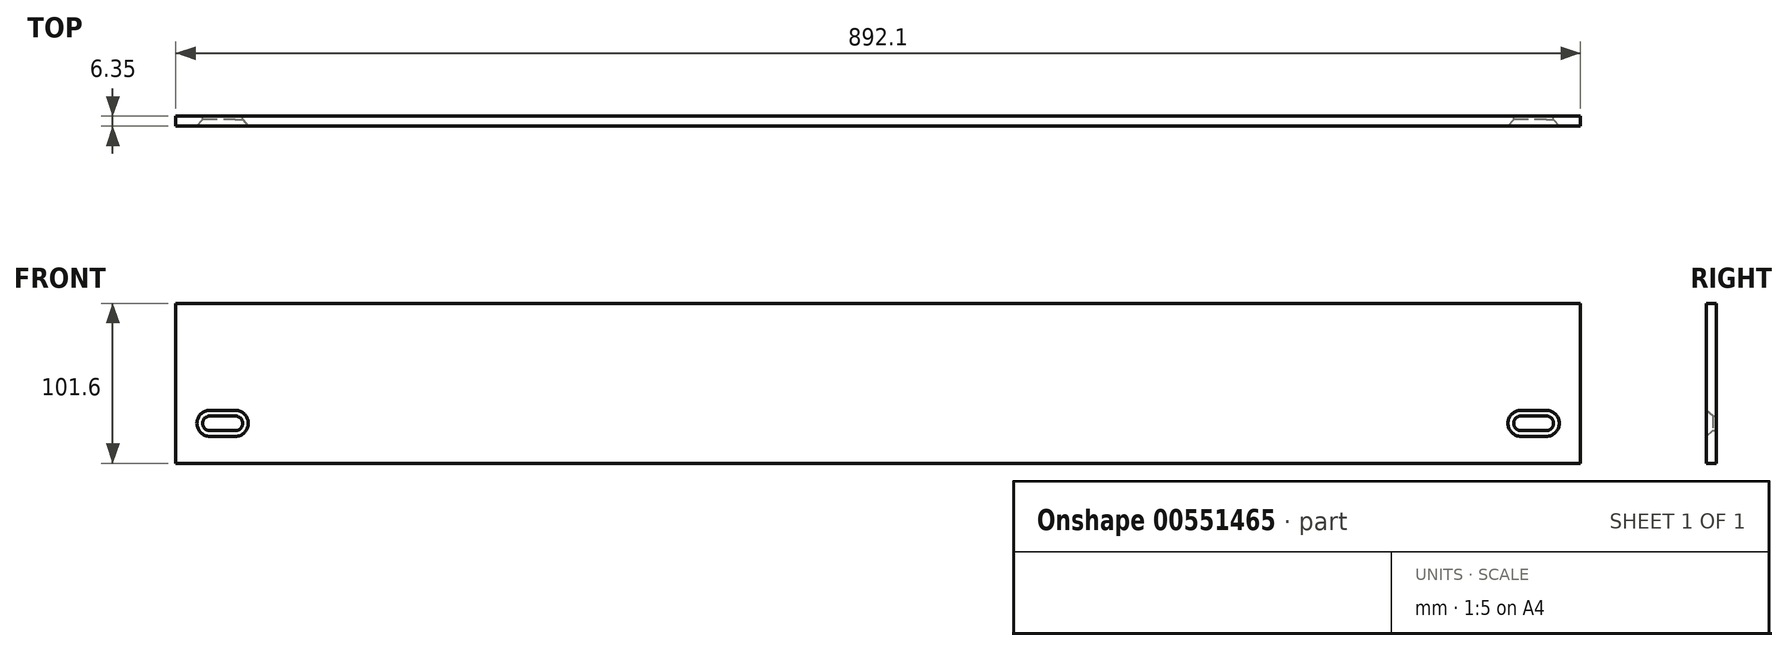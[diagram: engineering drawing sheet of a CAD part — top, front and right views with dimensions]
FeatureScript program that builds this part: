
annotation { "Feature Type Name" : "Feature", "Feature Type Description" : "" }
export const myFeature = defineFeature(function(context is Context, id is Id, definition is map)
    precondition{}
    {
        {
            var Q0;
            Q0=qCreatedBy(makeId("Front.planeOp"),FACE);
            var sketch = newSketch(context, id + "F0", { "sketchPlane" : qUnion([Q0])});
            skLineSegment(sketch, "E0", {"start": v(-446.05, -50.8) * mm, "end": v(-446.05, 50.8) * mm});
            skLineSegment(sketch, "E1", {"start": v(446.05, -50.8) * mm, "end": v(-446.05, -50.8) * mm});
            skLineSegment(sketch, "E2", {"start": v(446.05, 50.8) * mm, "end": v(-446.05, 50.8) * mm});
            skLineSegment(sketch, "E3", {"start": v(446.05, -50.8) * mm, "end": v(446.05, 50.8) * mm});
            skArc(sketch, "E4", {"start": v(-424.41, -20.76) * mm, "mid": v(-429.05, -25.4) * mm, "end": v(-424.41, -30.04) * mm});
            skArc(sketch, "E5", {"start": v(-408.24, -30.04) * mm, "mid": v(-403.6, -25.4) * mm, "end": v(-408.24, -20.76) * mm});
            skArc(sketch, "E6", {"start": v(408.28, -20.76) * mm, "mid": v(403.65, -25.4) * mm, "end": v(408.28, -30.04) * mm});
            skArc(sketch, "E7", {"start": v(424.37, -30.04) * mm, "mid": v(429, -25.4) * mm, "end": v(424.37, -20.76) * mm});
            skLineSegment(sketch, "E8", {"start": v(408.28, -20.76) * mm, "end": v(424.37, -20.76) * mm});
            skLineSegment(sketch, "E9", {"start": v(424.37, -30.04) * mm, "end": v(408.28, -30.04) * mm});
            skLineSegment(sketch, "E10", {"start": v(-424.41, -20.76) * mm, "end": v(-408.24, -20.76) * mm});
            skLineSegment(sketch, "E11", {"start": v(-408.24, -30.04) * mm, "end": v(-424.41, -30.04) * mm});
            skSolve(sketch);
        }
        {
            var Q0;
            Q0=makeQuery(id+"F0.imprint","IMPRINT",FACE,{"disambiguationData":[TD([[makeQuery(id+"F0.imprint","IMPRINT",EDGE,{"derivedFrom":sQuery(id+"F0.wireOp",EDGE,"E0")}),-1.0]])]});
            extrude(context, id + "F1", {"entities" : qUnion([Q0]), "depth" : 6.35 * mm, "offsetDistance" : 25.4 * mm});
        }
        {
            var Q0;
            Q0=makeQuery(id+"F1.opExtrude","CAP_EDGE",EDGE,{"disambiguationData":[OSD([sQuery(id+"F0.wireOp",EDGE,"E10")])],"isStart":false});
            var Q1;
            Q1=makeQuery(id+"F1.opExtrude","CAP_EDGE",EDGE,{"disambiguationData":[OSD([sQuery(id+"F0.wireOp",EDGE,"E8")])],"isStart":false});
            chamfer(context, id + "F2", {"entities" : qUnion([Q0, Q1]), "chamferType" : ChamferType.OFFSET_ANGLE, "width" : 4.17 * mm, "oppositeDirection" : true, "angle" : 41 * degree, "tangentPropagation" : true});
        }
    });
